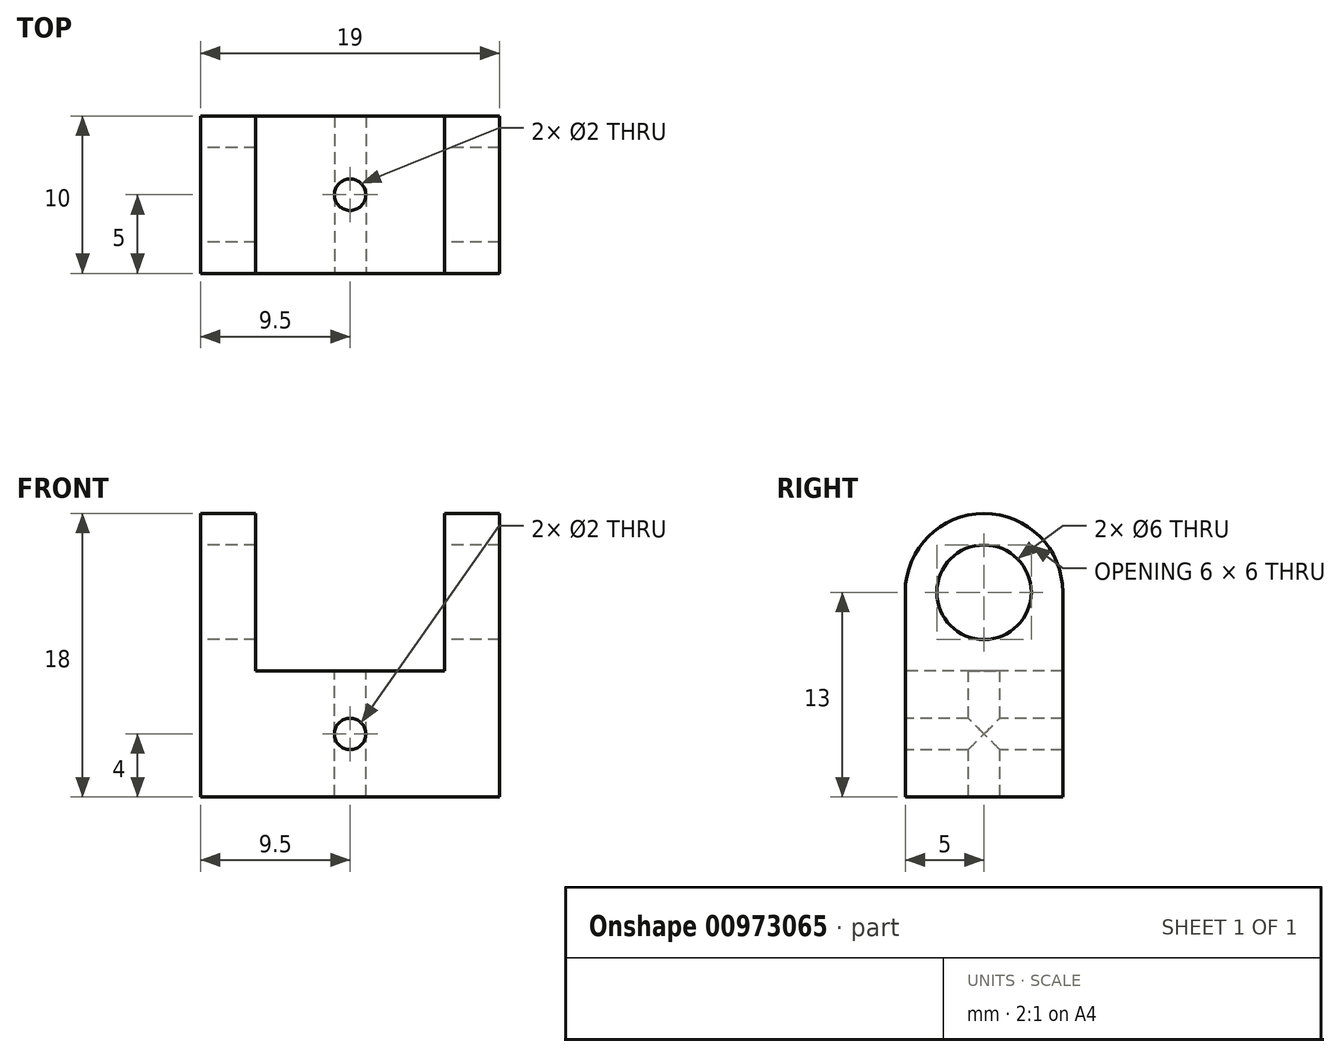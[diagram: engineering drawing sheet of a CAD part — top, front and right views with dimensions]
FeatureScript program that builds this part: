
annotation { "Feature Type Name" : "Feature", "Feature Type Description" : "" }
export const myFeature = defineFeature(function(context is Context, id is Id, definition is map)
    precondition{}
    {
        {
            var Q0;
            Q0=qCreatedBy(makeId("Top.planeOp"),FACE);
            var sketch = newSketch(context, id + "F0", { "sketchPlane" : qUnion([Q0]), "disableImprinting" : false});
            skLineSegment(sketch, "E0.bottom", {"start": v(9.5, -5) * mm, "end": v(-9.5, -5) * mm});
            skLineSegment(sketch, "E0.top", {"start": v(9.5, 5) * mm, "end": v(-9.5, 5) * mm});
            skLineSegment(sketch, "E0.left", {"start": v(9.5, -5) * mm, "end": v(9.5, 5) * mm});
            skLineSegment(sketch, "E0.right", {"start": v(-9.5, -5) * mm, "end": v(-9.5, 5) * mm});
            skPoint(sketch, "E0.middle", {"position": v(0, 0) * mm});
            skLineSegment(sketch, "E1.bottom", {"start": v(6, 5) * mm, "end": v(9.5, 5) * mm});
            skLineSegment(sketch, "E1.top", {"start": v(6, -5) * mm, "end": v(9.5, -5) * mm});
            skLineSegment(sketch, "E1.left", {"start": v(6, 5) * mm, "end": v(6, -5) * mm});
            skLineSegment(sketch, "E1.right", {"start": v(9.5, 5) * mm, "end": v(9.5, -5) * mm});
            skLineSegment(sketch, "E2", {"start": v(0, 5) * mm, "end": v(0, -5) * mm, "construction": true});
            skLineSegment(sketch, "E3.MirrorCS", {"start": v(-6, 5) * mm, "end": v(-9.5, 5) * mm});
            skLineSegment(sketch, "E4.MirrorCS", {"start": v(-9.5, 5) * mm, "end": v(-9.5, -5) * mm});
            skLineSegment(sketch, "E5.MirrorCS", {"start": v(-6, 5) * mm, "end": v(-6, -5) * mm});
            skLineSegment(sketch, "E6.MirrorCS", {"start": v(-6, -5) * mm, "end": v(-9.5, -5) * mm});
            skSolve(sketch);
        }
        {
            var Q0;
            {var subQ0=sQuery(id+"F0.wireOp",EDGE,"E1.left");Q0=makeQuery(id+"F0.imprint","IMPRINT",FACE,{"disambiguationData":[TD([[makeQuery(id+"F0.imprint","IMPRINT",EDGE,{"derivedFrom":subQ0}),-1.0]])]});}
            extrude(context, id + "F1", {"entities" : qUnion([Q0]), "depth" : 8 * mm, "offsetDistance" : 25 * mm});
        }
        {
            var Q0;
            {var subQ0=sQuery(id+"F0.wireOp",EDGE,"E0.right");Q0=makeQuery(id+"F0.imprint","IMPRINT",FACE,{"disambiguationData":[TD([[makeQuery(id+"F0.imprint","IMPRINT",EDGE,{"derivedFrom":subQ0}),-1.0]])]});}
            var Q1;
            {var subQ2=sQuery(id+"F0.wireOp",EDGE,"E0.left");Q1=makeQuery(id+"F0.imprint","IMPRINT",FACE,{"disambiguationData":[TD([[makeQuery(id+"F0.imprint","IMPRINT",EDGE,{"derivedFrom":subQ2}),1.0]])]});}
            var Q2;
            {Q2=qUnion([sQuery(id+"F0.wireOp",EDGE,"E0.bottom"),sQuery(id+"F0.wireOp",EDGE,"E0.top"),sQuery(id+"F0.wireOp",EDGE,"E0.left"),sQuery(id+"F0.wireOp",EDGE,"E0.right"),sQuery(id+"F0.wireOp",EDGE,"E1.bottom"),sQuery(id+"F0.wireOp",EDGE,"E1.top"),sQuery(id+"F0.wireOp",EDGE,"E1.left"),sQuery(id+"F0.wireOp",EDGE,"E1.right"),sQuery(id+"F0.wireOp",EDGE,"E0.right"),sQuery(id+"F0.wireOp",EDGE,"E3.MirrorCS"),sQuery(id+"F0.wireOp",EDGE,"E4.MirrorCS"),sQuery(id+"F0.wireOp",EDGE,"E5.MirrorCS"),sQuery(id+"F0.wireOp",EDGE,"E6.MirrorCS")]);}
            extrude(context, id + "F2", {"entities" : qUnion([Q0, Q1]), "operationType" : NewBodyOperationType.ADD, "surfaceEntities" : qUnion([Q2]), "depth" : 18 * mm, "offsetDistance" : 25 * mm});
        }
        {
            var Q0;
            Q0=makeQuery(id+"F2.opExtrude","SWEPT_FACE",FACE,{"disambiguationData":[OSD([sQuery(id+"F0.wireOp",EDGE,"E0.right")])]});
            var sketch = newSketch(context, id + "F3", { "sketchPlane" : qUnion([Q0]), "disableImprinting" : false});
            skCircle(sketch, "E7", {"center": v(0, 13) * mm, "radius": 3 * mm});
            skArc(sketch, "E8", {"start": v(5, 13) * mm, "mid": v(0, 18) * mm, "end": v(-5, 13) * mm});
            skLineSegment(sketch, "E9", {"start": v(-5, 13) * mm, "end": v(-5, 9) * mm});
            skLineSegment(sketch, "E10", {"start": v(-5, 18) * mm, "end": v(-5, 9) * mm});
            skLineSegment(sketch, "E11", {"start": v(0, 18) * mm, "end": v(0, 11.95) * mm, "construction": true});
            skLineSegment(sketch, "E12", {"start": v(-5, 18) * mm, "end": v(0, 18) * mm});
            skLineSegment(sketch, "E13.MirrorCS", {"start": v(5, 18) * mm, "end": v(0, 18) * mm});
            skLineSegment(sketch, "E14.MirrorCS", {"start": v(5, 18) * mm, "end": v(5, 9) * mm});
            skLineSegment(sketch, "E15.MirrorCS", {"start": v(5, 13) * mm, "end": v(5, 9) * mm});
            skSolve(sketch);
        }
        {
            var Q0;
            Q0 = qSketchRegion(id + "F3", true);
            extrude(context, id + "F4", {"entities" : qUnion([Q0]), "operationType" : NewBodyOperationType.REMOVE, "flatOperationType" : FlatOperationType.REMOVE, "endBound" : BoundingType.THROUGH_ALL, "oppositeDirection" : true, "depth" : 25 * mm, "offsetDistance" : 25 * mm, "domain" : OperationDomain.MODEL});
        }
        {
            var Q0;
            {var subQ0=sQuery(id+"F0.wireOp",EDGE,"E0.bottom");Q0=makeQuery(id+"F2.boolean.opBoolean","MERGE",FACE,{"derivedFrom":[makeQuery(id+"F1.opExtrude","SWEPT_FACE",FACE,{"disambiguationData":[OSD([subQ0])]}),makeQuery(id+"F2.opExtrude","SWEPT_FACE",FACE,{"disambiguationData":[OSD([subQ0]),TDD([makeQuery(id+"F0.imprint","IMPRINT",EDGE,{"disambiguationData":[TD([[makeQuery(id+"F0.imprint","INTERSECT",VERTEX,{"derivedFrom":[subQ0,sQuery(id+"F0.wireOp",EDGE,"E0.right")]}),1.0]])],"derivedFrom":subQ0})])]}),makeQuery(id+"F2.opExtrude","SWEPT_FACE",FACE,{"disambiguationData":[OSD([subQ0]),TDD([makeQuery(id+"F0.imprint","IMPRINT",EDGE,{"disambiguationData":[TD([[makeQuery(id+"F0.imprint","INTERSECT",VERTEX,{"derivedFrom":[subQ0,sQuery(id+"F0.wireOp",EDGE,"E1.left")]}),1.0]])],"derivedFrom":subQ0})])]})]});}
            var sketch = newSketch(context, id + "F5", { "sketchPlane" : qUnion([Q0])});
            skCircle(sketch, "E16", {"center": v(0, 4) * mm, "radius": 1 * mm});
            skLineSegment(sketch, "E17", {"start": v(0, 0) * mm, "end": v(0, 8) * mm, "construction": true});
            skSolve(sketch);
        }
        {
            var Q0;
            Q0 = qSketchRegion(id + "F5", true);
            extrude(context, id + "F6", {"entities" : qUnion([Q0]), "operationType" : NewBodyOperationType.REMOVE, "endBound" : BoundingType.THROUGH_ALL, "oppositeDirection" : true, "depth" : 25 * mm, "offsetDistance" : 25 * mm});
        }
        {
            var Q0;
            Q0=makeQuery(id+"F1.opExtrude","CAP_FACE",FACE,{"disambiguationData":[OSD([sQuery(id+"F0.wireOp",EDGE,"E0.bottom"),sQuery(id+"F0.wireOp",EDGE,"E0.top"),sQuery(id+"F0.wireOp",EDGE,"E1.left"),sQuery(id+"F0.wireOp",EDGE,"E5.MirrorCS")])],"isStart":false});
            var sketch = newSketch(context, id + "F7", { "sketchPlane" : qUnion([Q0])});
            skCircle(sketch, "E18", {"center": v(0, 0) * mm, "radius": 1 * mm});
            skSolve(sketch);
        }
        {
            var Q0;
            Q0 = qSketchRegion(id + "F7", true);
            extrude(context, id + "F8", {"entities" : qUnion([Q0]), "operationType" : NewBodyOperationType.REMOVE, "endBound" : BoundingType.THROUGH_ALL, "oppositeDirection" : true, "depth" : 25 * mm, "offsetDistance" : 25 * mm});
        }
    });
